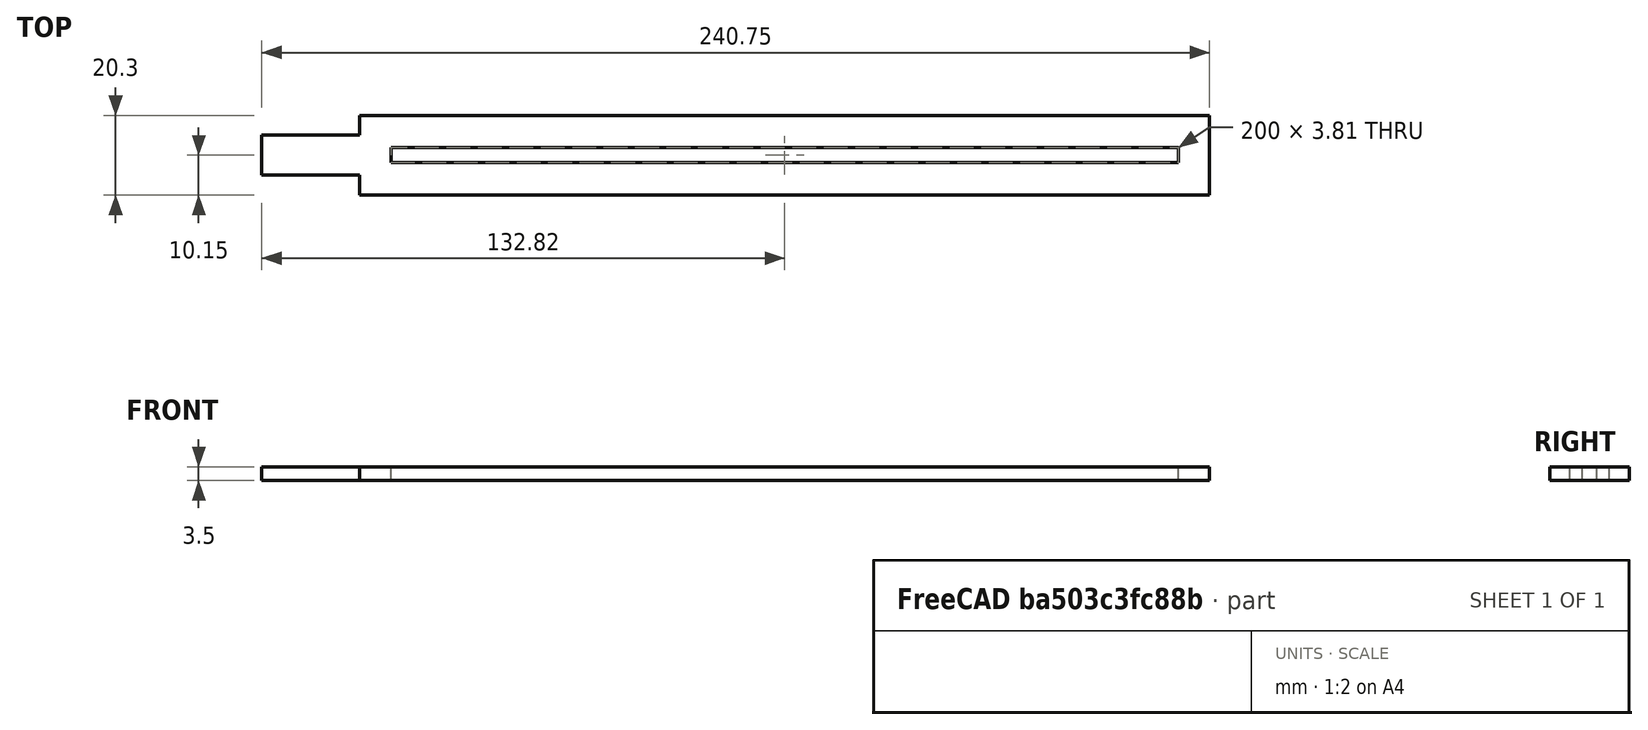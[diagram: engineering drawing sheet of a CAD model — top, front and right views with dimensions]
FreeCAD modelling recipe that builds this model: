
FCSTD DOCUMENT  (FreeCAD 0.21R33668 +26 (Git))
Label: MagnetoPot
License: All rights reserved
LicenseURL: http://en.wikipedia.org/wiki/All_rights_reserved
objects: Sketcher::SketchObject×2, PartDesign::Pad×1, PartDesign::Body×1
note: 5 computed .brp shape members not serialized (recipe doc carries the construction recipe); baked Part::Feature solids carry a one-line shape summary decoded from their .brp

FEATURE [Sketcher::SketchObject] Sketch
  FullyConstrained = true
  MapMode = 5
  Support = -> [XY_Plane]
  sketch-geometry (17):
    g0: LineSegment StartX=0 StartY=0 StartZ=0 EndX=215.86 EndY=0 EndZ=0
    g1: LineSegment StartX=215.86 StartY=0 StartZ=0 EndX=215.86 EndY=20.3 EndZ=0
    g2: LineSegment StartX=215.86 StartY=20.3 StartZ=0 EndX=0 EndY=20.3 EndZ=0
    g3: LineSegment StartX=0 StartY=20.3 StartZ=0 EndX=0 EndY=0 EndZ=0
    g4: LineSegment StartX=7.93 StartY=8.245 StartZ=0 EndX=207.93 EndY=8.245 EndZ=0
    g5: LineSegment StartX=207.93 StartY=8.245 StartZ=0 EndX=207.93 EndY=12.055 EndZ=0
    g6: LineSegment StartX=207.93 StartY=12.055 StartZ=0 EndX=7.93 EndY=12.055 EndZ=0
    g7: LineSegment StartX=7.93 StartY=12.055 StartZ=0 EndX=7.93 EndY=8.245 EndZ=0
    g8: GeomPoint X=107.93 Y=10.15 Z=0
    g9: LineSegment StartX=-24.89 StartY=15.23 StartZ=0 EndX=0 EndY=15.23 EndZ=0
    g10: LineSegment StartX=0 StartY=15.23 StartZ=0 EndX=0 EndY=5.07 EndZ=0
    g11: LineSegment StartX=0 StartY=5.07 StartZ=0 EndX=-24.89 EndY=5.07 EndZ=0
    g12: LineSegment StartX=-24.89 StartY=5.07 StartZ=0 EndX=-24.89 EndY=15.23 EndZ=0
    g13: LineSegment StartX=0 StartY=20.3 StartZ=0 EndX=0 EndY=15.23 EndZ=0
    g14: LineSegment StartX=0 StartY=5.07 StartZ=0 EndX=0 EndY=0 EndZ=0
    g15: GeomPoint X=0 Y=10.15 Z=0
    g16: LineSegment StartX=215.86 StartY=20.3 StartZ=0 EndX=215.86 EndY=0 EndZ=0
  constraints (42):
    c: Coincident(g0,g1)
    c: Coincident(g1,g2)
    c: Coincident(g2,g3)
    c: Coincident(g3,g0)
    c: Horizontal(g0)
    c: Horizontal(g2)
    c: Vertical(g1)
    c: Vertical(g3)
    c: Coincident(g0,g-1)
    c: DistanceX(g2,g2) = 215.86  'PartLength'
    c: DistanceY(g3,g3) = 20.3  'PartWidth'
    c: Coincident(g4,g5)
    c: Coincident(g5,g6)
    c: Coincident(g6,g7)
    c: Coincident(g7,g4)
    c: Horizontal(g4)
    c: Horizontal(g6)
    c: Vertical(g5)
    c: Vertical(g7)
    c: Symmetric(g2,g0,g8)
    c: Symmetric(g4,g5,g8)
    c: DistanceY(g5,g5) = 3.81  'ActiveWidth'
    c: DistanceX(g6,g6) = 200  'ActiveLength'
    c: Coincident(g9,g10)
    c: Coincident(g10,g11)
    c: Coincident(g11,g12)
    c: Coincident(g12,g9)
    c: Horizontal(g9)
    c: Horizontal(g11)
    c: Vertical(g10)
    c: Vertical(g12)
    c: Coincident(g13,g2)
    c: Coincident(g13,g9)
    c: Coincident(g14,g11)
    c: Coincident(g14,g0)
    c: Symmetric(g2,g0,g15)
    c: Symmetric(g9,g11,g15)
    c: DistanceX(g9,g9) = 24.89  'TailLength'
    c: DistanceY(g12,g12) = 10.16  'TailWidth'
    c: Coincident(g16,g2)
    c: Coincident(g16,g0)
    c: DistanceY(g0,g4) = 8.245  'EdgeToActiveWidth'
FEATURE [PartDesign::Pad] Pad
  Direction = (0,0,1)
  Length = 3.5
  Length2 = 10
  Profile = -> Sketch
  ReferenceAxis = -> Sketch [N_Axis]
  Type = 0
FEATURE [Sketcher::SketchObject] Sketch001
  ExternalGeometry = -> [Pad]
  FullyConstrained = true
  MapMode = 5
  Placement = pos=(0,0,0) rot=(1,0,0;1.5708rad)
  Support = -> [Pad]
  constraints (1):
    c: DistanceY(g-1,g-3) = 3.5  'Height'
FEATURE [PartDesign::Body] Body  label="MP1_L_0200_103_5_ST"
  Group = -> [Sketch,Pad,Sketch001]
  Origin = -> Origin
  Tip = -> Pad
